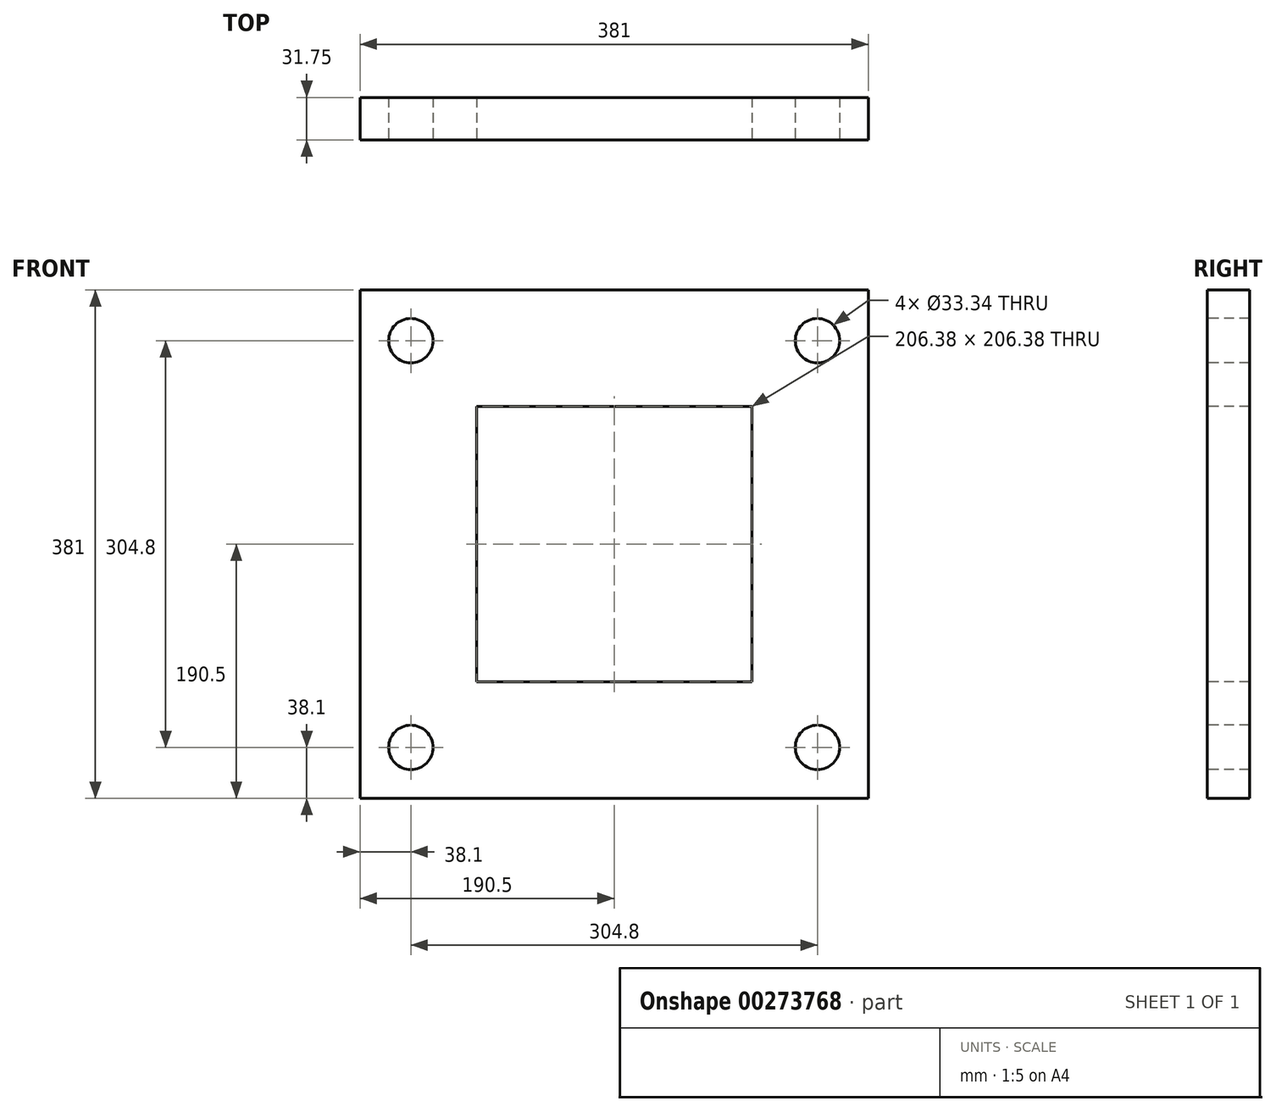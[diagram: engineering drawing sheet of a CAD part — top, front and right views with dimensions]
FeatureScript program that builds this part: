
annotation { "Feature Type Name" : "Feature", "Feature Type Description" : "" }
export const myFeature = defineFeature(function(context is Context, id is Id, definition is map)
    precondition{}
    {
        {
            var Q0;
            Q0=qCreatedBy(makeId("Front.planeOp"),FACE);
            var sketch = newSketch(context, id + "F0", { "sketchPlane" : qUnion([Q0])});
            skLineSegment(sketch, "E0.bottom", {"start": v(190.5, 190.5) * mm, "end": v(-190.5, 190.5) * mm});
            skLineSegment(sketch, "E0.top", {"start": v(190.5, -190.5) * mm, "end": v(-190.5, -190.5) * mm});
            skLineSegment(sketch, "E0.left", {"start": v(190.5, 190.5) * mm, "end": v(190.5, -190.5) * mm});
            skLineSegment(sketch, "E0.right", {"start": v(-190.5, 190.5) * mm, "end": v(-190.5, -190.5) * mm});
            skPoint(sketch, "E0.middle", {"position": v(0, 0) * mm});
            skLineSegment(sketch, "E1.bottom", {"start": v(-152.4, 152.4) * mm, "end": v(152.4, 152.4) * mm});
            skLineSegment(sketch, "E1.top", {"start": v(-152.4, -152.4) * mm, "end": v(152.4, -152.4) * mm});
            skLineSegment(sketch, "E1.left", {"start": v(-152.4, 152.4) * mm, "end": v(-152.4, -152.4) * mm});
            skLineSegment(sketch, "E1.right", {"start": v(152.4, 152.4) * mm, "end": v(152.4, -152.4) * mm});
            skLineSegment(sketch, "E2.bottom", {"start": v(-103.19, 103.19) * mm, "end": v(103.19, 103.19) * mm});
            skLineSegment(sketch, "E2.top", {"start": v(-103.19, -103.19) * mm, "end": v(103.19, -103.19) * mm});
            skLineSegment(sketch, "E2.left", {"start": v(-103.19, 103.19) * mm, "end": v(-103.19, -103.19) * mm});
            skLineSegment(sketch, "E2.right", {"start": v(103.19, 103.19) * mm, "end": v(103.19, -103.19) * mm});
            skSolve(sketch);
        }
        {
            var Q0;
            Q0=makeQuery(id+"F0.imprint","IMPRINT",FACE,{"disambiguationData":[TD([[makeQuery(id+"F0.imprint","IMPRINT",EDGE,{"derivedFrom":sQuery(id+"F0.wireOp",EDGE,"E0.bottom")}),1.0]])]});
            var Q1;
            Q1=makeQuery(id+"F0.imprint","IMPRINT",FACE,{"disambiguationData":[TD([[makeQuery(id+"F0.imprint","IMPRINT",EDGE,{"derivedFrom":sQuery(id+"F0.wireOp",EDGE,"E1.bottom")}),-1.0]])]});
            extrude(context, id + "F1", {"entities" : qUnion([Q0, Q1]), "oppositeDirection" : true, "depth" : 31.75 * mm});
        }
        {
            var Q0;
            Q0=sQuery(id+"F0.wireOp",VERTEX,"E1.left.start");
            var Q1;
            Q1=sQuery(id+"F0.wireOp",VERTEX,"E1.bottom.end");
            var Q2;
            Q2=sQuery(id+"F0.wireOp",VERTEX,"E1.top.end");
            var Q3;
            Q3=sQuery(id+"F0.wireOp",VERTEX,"E1.top.start");
            var Q4;
            Q4=makeQuery(id+"F1.opExtrude","SWEPT_BODY",BODY,{"disambiguationData":[OSD([sQuery(id+"F0.wireOp",EDGE,"E0.bottom"),sQuery(id+"F0.wireOp",EDGE,"E0.top"),sQuery(id+"F0.wireOp",EDGE,"E0.left"),sQuery(id+"F0.wireOp",EDGE,"E0.right")])]});
            hole(context, id + "F2", {"style" : HoleStyle.SIMPLE, "endStyle" : HoleEndStyle.THROUGH, "holeDiameter" : 33.34 * mm, "tappedDepth" : 12.7 * mm, "tapClearance" : 3, "locations" : qUnion([Q0, Q1, Q2, Q3]), "scope" : qUnion([Q4])});
        }
    });
